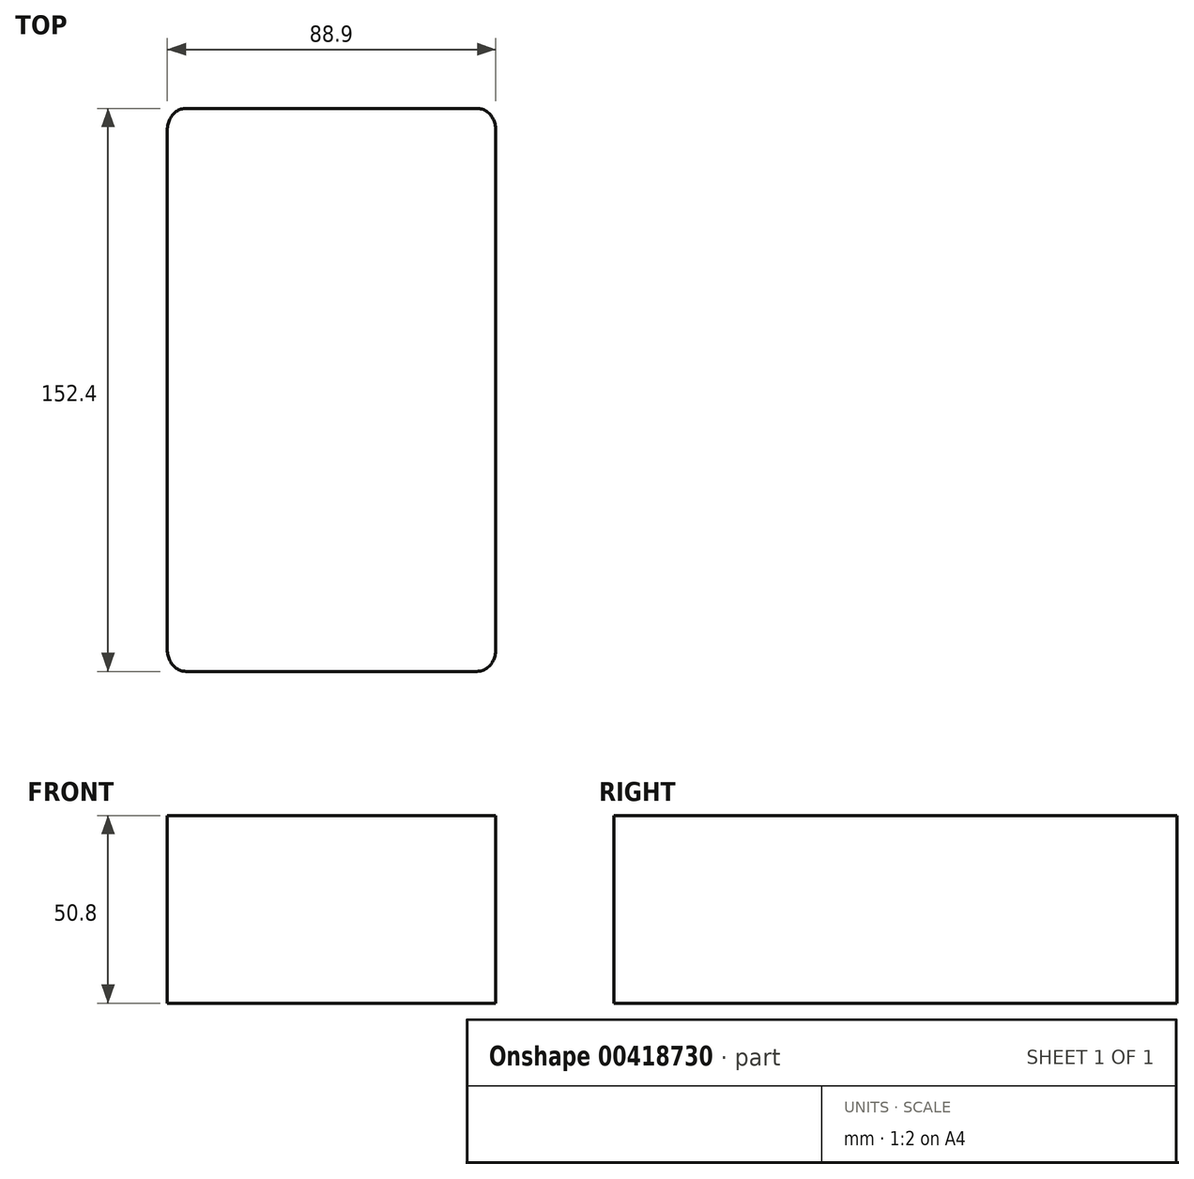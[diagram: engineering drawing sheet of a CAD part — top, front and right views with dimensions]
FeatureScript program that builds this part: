
annotation { "Feature Type Name" : "Feature", "Feature Type Description" : "" }
export const myFeature = defineFeature(function(context is Context, id is Id, definition is map)
    precondition{}
    {
        {
            var Q0;
            Q0=qCreatedBy(makeId("Top.planeOp"),FACE);
            var sketch = newSketch(context, id + "F0", { "sketchPlane" : qUnion([Q0])});
            skLineSegment(sketch, "E0.0.0", {"start": v(-38.64, 45.88) * mm, "end": v(-38.64, -94.79) * mm});
            skEllipticalArc(sketch, "E0.0.1", {});
            skLineSegment(sketch, "E0.0.2", {"start": v(-33.56, -100.65) * mm, "end": v(45.18, -100.65) * mm});
            skEllipticalArc(sketch, "E0.0.3", {});
            skLineSegment(sketch, "E0.0.4", {"start": v(50.26, -94.79) * mm, "end": v(50.26, 45.88) * mm});
            skEllipticalArc(sketch, "E0.0.5", {});
            skLineSegment(sketch, "E0.0.6", {"start": v(45.18, 51.75) * mm, "end": v(-33.56, 51.75) * mm});
            skEllipticalArc(sketch, "E0.0.7", {});
            const initialGuessF0  = {"E0.0.1": [-0.03356004935771227, -0.09478821387193552, 0, 1, 0.0058658787349666, 0.00508, 1.5707963267948966, 3.141592653589793], "E0.0.3": [0.04517995064228773, -0.09478821387193552, 0, -1, 0.0058658787349666, 0.00508, 0, 1.5707963267948966], "E0.0.5": [0.04517995064228773, 0.045880028658131275, 0, -1, 0.0058658787349665995, 0.00508, 1.5707963267948966, 3.141592653589793], "E0.0.7": [-0.03356004935771227, 0.04588002865813126, 0, 1, 0.0058658787349665995, 0.00508, 0, 1.5707963267948966]};
            skSetInitialGuess(sketch, initialGuessF0);
            skSolve(sketch);
        }
        {
            var Q0;
            Q0=makeQuery(id+"F0.imprint","IMPRINT",FACE,{"disambiguationData":[TD([[makeQuery(id+"F0.imprint","IMPRINT",EDGE,{"derivedFrom":sQuery(id+"F0.wireOp",EDGE,"E0.0.0")}),1.0]])]});
            extrude(context, id + "F1", {"entities" : qUnion([Q0]), "oppositeDirection" : true, "depth" : 50.8 * mm});
        }
    });
